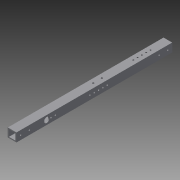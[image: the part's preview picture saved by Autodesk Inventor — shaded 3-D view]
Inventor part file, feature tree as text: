
AUTODESK INVENTOR PART (.ipt)
format: ipt  version: 2014 (Build 180170000, 170)  size: 148,992 bytes
history: native  units: in
note: dims shown in document units (in); Inventor stores cm internally (conversion verified against a paired STEP export)
features: extrude x3, sketch x3
ambient origin geometry x8: Origin, YZ Plane, XZ Plane, XY Plane, X Axis, Y Axis, Z Axis, Center Point
bodies: Solid1 (feature_tree)
feature tree (6):
  extrude  "Extrusion1"  Depth=1.0in
  extrude  "Extrusion2"  Depth=18.0in TaperAngle=0.0deg
  extrude  "Extrusion3"  Depth=18.0in
  sketch  "Sketch1"  dims[d0=1.0in d1=1.0in]
  sketch  "Sketch2"  dims[d2=0.125in d3=18.0in d4=0.0in]
  sketch  "Sketch3"  dims[d5=0.163in d6=0.5in d7=0.5in d8=0.7874in d10=1.0in d11=0.3937in d13=1.0in d15=0.5in d16=2.5in d17=0.7874in d19=0.5in d20=0.3937in d22=1.0in d24=0.5938in d25=1.0in d26=0.5in d27=4.0in d28=0.5in d29=1.9685in d31=0.5in d32=0.3937in d34=1.0in d36=0.5in d37=0.5in d38=0.7874in d40=1.0in d41=0.3937in d43=1.0in d45=18.0in d46=0.0in d47=0.196in d48=9.375in d49=0.5in d50=0.7874in d52=1.0in d53=0.3937in d55=1.0in d57=0.163in d58=0.5in d59=2.0in d60=1.9685in d62=0.5in d63=0.3937in d65=1.0in d67=18.0in d68=0.0in]
